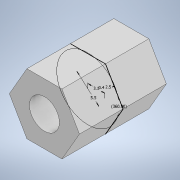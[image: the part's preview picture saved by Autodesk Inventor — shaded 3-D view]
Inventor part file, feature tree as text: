
AUTODESK INVENTOR PART (.ipt)
format: ipt  version: 2022 (Build 260153000, 153)  size: 120,320 bytes
history: native  units: mm
features: extrude x2, sketch x1
ambient origin geometry x8: Origin, YZ Plane, XZ Plane, XY Plane, X Axis, Y Axis, Z Axis, Center Point
bodies: Solid1 (feature_tree)
feature tree (3):
  sketch  "Sketch1"  dims[d0=5.5mm d2=3.1mm d3=60.0mm d5=360.0deg d7=0.4mm d8=2.5mm d9=8.0mm d10=0.0mm d11=8.0mm d12=0.0mm d4=0.5mm]
  extrude  "Extrusion1"  Depth=8.0mm
  extrude  "Extrusion2"  Depth=8.0mm TaperAngle=360.0deg
